# Revit family: Salda Indoor Horizontal AHU.Smarty Series
name_source: partatom
category: Mechanical Equipment
revit_build: Autodesk Revit 2016 (Build: 20150220_1215(x64)
units: mm (PartAtom-declared; Revit-internal decimal feet)

## family parameters
Always vertical = Yes
Cut with Voids When Loaded = No
OmniClass Number = 23.75.35.14.11
OmniClass Title = Built-Up Indoor Air Handling Units
Part Type = Normal
Room Calculation Point = No
Round Connector Dimension = Use Diameter
Shared = No
Work Plane-Based = No

## types (6) — shared parameters
Cover Height = 16 mm  [stored 0.0524934 ft]
Manufacturer = Salda
URL = http://salda.lt
Voltage = 230 V

## per-type parameters (varying)
| type | Connector Center Height | Connector Length | Connector Side Offset | Current | Drainage Pipe Offset 1 | Drainage Pipe Offset 2 | Electric Box | Maximum Flow Rate | Module Height | Module Length | Module Width | Overall Height | Overall Length | Overall Width | Power | Service Zone Height | Type | Unit Mass |
| Smarty 3X P 1.1 | 170 mm  [stored 0.557743 ft] | 78 mm | 128 mm  [stored 0.419948 ft] | 2 A | 258 mm  [stored 0.846457 ft] | 408 mm | No | 350.0 m³/h | 318 mm  [stored 1.04331 ft] | 1225 mm  [stored 4.01903 ft] | 685 mm | 324 mm  [stored 1.06299 ft] | 1380 mm  [stored 4.52756 ft] | 685 mm | 170 W | 477 mm  [stored 1.56496 ft] | 3 | 53.00 kg |
| Smarty 4X P 1.1 | 170 mm  [stored 0.557743 ft] | 78 mm | 128 mm  [stored 0.419948 ft] | 2 A | 258 mm  [stored 0.846457 ft] | 408 mm | Yes | 595.0 m³/h | 318 mm  [stored 1.04331 ft] | 1225 mm  [stored 4.01903 ft] | 685 mm | 324 mm  [stored 1.06299 ft] | 1380 mm  [stored 4.52756 ft] | 685 mm | 420 W | 477 mm  [stored 1.56496 ft] | 4 | 53.00 kg |
| Smarty 2X P 1.2 | 137 mm  [stored 0.449475 ft] | 39 mm | 115 mm  [stored 0.377297 ft] | 1 A | 202 mm  [stored 0.66273 ft] | 326 mm  [stored 1.06955 ft] | No | 219.0 m³/h | 244 mm  [stored 0.800525 ft] | 1009 mm  [stored 3.31037 ft] | 590 mm  [stored 1.9357 ft] | 250 mm | 1086 mm  [stored 3.56299 ft] | 590 mm  [stored 1.9357 ft] | 100 W | 366 mm  [stored 1.20079 ft] | 2 | 30.00 kg |
| Smarty 2X P 1.1 | 137 mm  [stored 0.449475 ft] | 39 mm | 115 mm  [stored 0.377297 ft] | 1 A | 202 mm  [stored 0.66273 ft] | 326 mm  [stored 1.06955 ft] | No | 219.0 m³/h | 244 mm  [stored 0.800525 ft] | 1009 mm  [stored 3.31037 ft] | 590 mm  [stored 1.9357 ft] | 250 mm | 1086 mm  [stored 3.56299 ft] | 590 mm  [stored 1.9357 ft] | 100 W | 366 mm  [stored 1.20079 ft] | 2 | 30.00 kg |
| Smarty 3X P 1.2 | 170 mm  [stored 0.557743 ft] | 78 mm | 128 mm  [stored 0.419948 ft] | 2 A | 258 mm  [stored 0.846457 ft] | 408 mm | No | 350.0 m³/h | 318 mm  [stored 1.04331 ft] | 1225 mm  [stored 4.01903 ft] | 685 mm | 324 mm  [stored 1.06299 ft] | 1380 mm  [stored 4.52756 ft] | 685 mm | 170 W | 477 mm  [stored 1.56496 ft] | 3 | 53.00 kg |
| Smarty 4X P 1.2 | 170 mm  [stored 0.557743 ft] | 78 mm | 128 mm  [stored 0.419948 ft] | 2 A | 258 mm  [stored 0.846457 ft] | 408 mm | Yes | 595.0 m³/h | 318 mm  [stored 1.04331 ft] | 1225 mm  [stored 4.01903 ft] | 685 mm | 324 mm  [stored 1.06299 ft] | 1380 mm  [stored 4.52756 ft] | 685 mm | 420 W | 477 mm  [stored 1.56496 ft] | 4 | 53.00 kg |

note: column(s) folded — value = type name in every type: Model

note: [stored X ft] marks values corroborated as IEEE doubles in the binary element streams (Revit-internal decimal feet)

## geometry (parser evidence)
native form markers: Sweep x10
no freeform markers — native parametric forms only
